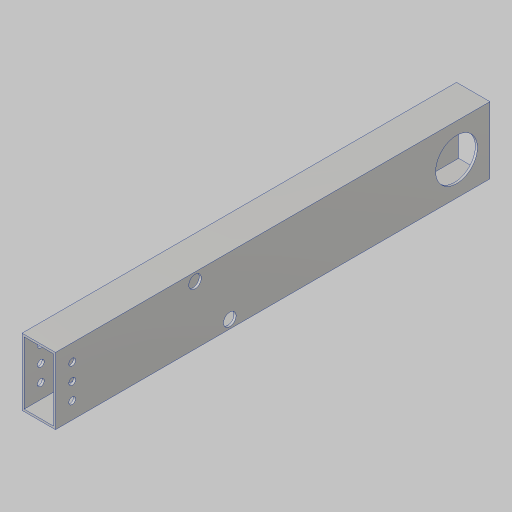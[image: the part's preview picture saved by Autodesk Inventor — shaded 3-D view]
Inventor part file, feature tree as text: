
AUTODESK INVENTOR PART (.ipt)
format: ipt  version: 2023.5 (Build 275446000, 446)  size: 151,552 bytes
history: native  units: in
note: dims shown in document units (in); Inventor stores cm internally (conversion verified against a paired STEP export)
features: projected_geometry x4, sketch x3, extrude x2, hole x2
ambient origin geometry x8: Origin, YZ Plane, XZ Plane, XY Plane, X Axis, Y Axis, Z Axis, Center Point
bodies: Solid1 (feature_tree)
feature tree (11):
  extrude  "Extrusion1"  Depth=1.25in
  extrude  "Extrusion3"  TaperAngle=0.0deg  [1 undecoded]
  hole  "Hole1"  [1 undecoded]
  hole  "Hole3"  [1 undecoded]
  sketch  "Sketch3"  dims[d4=0.0in d8=1.25in]
  sketch  "Sketch4"  dims[d9=1.0in d10=0.0in d11=0.0in]
  sketch  "Sketch6"  dims[d12=0.5in d13=0.5in d14=0.5in d15=0.201in d16=0.75in d17=0.385in d18=0.25in d19=0.5635in d20=1.0in d21=0.8108in d35=6.0in d36=0.3793in d37=8.0in d38=2.0in d39=0.378in d40=0.5in d41=0.375in d42=0.75in d43=0.385in d44=0.25in d45=0.5635in d46=1.0in d47=0.8108in]
  projected_geometry  "Project Cut Edges1"
  projected_geometry  "Project Cut Edges3"
  projected_geometry  "Project Cut Edges4"
  projected_geometry  "Project Cut Edges5"
note: 3 required parameter values undecoded (feature->parameter linkage not recoverable at this tier; creation-order binding heuristic only, values carry confidence <= 0.55)
